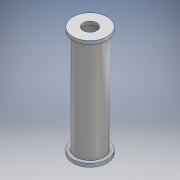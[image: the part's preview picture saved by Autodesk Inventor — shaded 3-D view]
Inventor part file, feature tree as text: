
AUTODESK INVENTOR PART (.ipt)
format: ipt  version: 2016 (Build 200138000, 138)  size: 128,512 bytes
history: native  units: mm
features: extrude x4, sketch x3, hole x2, other x1
ambient origin geometry x8: Origin, YZ Plane, XZ Plane, XY Plane, X Axis, Y Axis, Z Axis, Center Point
bodies: Body1 (feature_tree)
feature tree (10):
  other  "ソリッド1"
  sketch  "スケッチ1"
  extrude  "押し出し1"  Depth=8.0mm
  extrude  "押し出し2"  Depth=4.001mm
  extrude  "押し出し3"  Depth=10.0mm
  sketch  "スケッチ3"
  extrude  "押し出し4"  Depth=30.0mm TaperAngle=0.0deg
  hole  "穴1"  [1 undecoded]
  hole  "穴2"  [1 undecoded]
  sketch  "スケッチ2"
note: 2 required parameter values undecoded (feature->parameter linkage not recoverable at this tier; creation-order binding heuristic only, values carry confidence <= 0.55)
